# Revit family: Дверь ТДО
name_source: partatom
category: Двери
revit_build: Autodesk Revit 2015 (Build: 20140223_1515(x64)
units: mm (PartAtom-declared; Revit-internal decimal feet)

## types (1)
- Дверь ТДО
    ADSK_URL страницы изделия = http://profholod.ru
    ADSK_Завод-изготовитель = ООО ПрофХолод
    ADSK_Обозначение = ООО ПрофХолод
    ADSK_Открывание = Пр
    URL = http://profholod.ru
    h_porog = 0 мм
    hn_polotno = 8 мм
    Аналитическая конструкция = <Нет>
    Внутренняя сторона = AISI 430-0,5
    Высота = 2200 мм
    Высота в свету = 2168 мм
    Высота порога = 0 мм
    Высота проема до монтажа = 2200 мм
    Высота ручки = 900 мм
    Группа модели = ТДО
    Замыкание стены = По основе
    Изготовитель = ООО ПрофХолод
    Изогнутый отбойник левый = Нет
    Изогнутый отбойник правый = Нет
    Иллюминатор стекло = Пластмасса, прозрачная
    Кирпич = ККС : КРК - к крипичной стене
    Коробка и наличники = RAL9003
    Металл = ККС : МК - к металлоконструкции
    Наружная сторона = RAL9003
    Описание = Двери технологические (ТДО)
    Петли левые = Нет
    Петли правые = Да
    Порог 40 = П : Порог 40
    Порог 40мм = Нет
    Порог 60 = П : Порог 60
    Порог 60мм = Нет
    Резиновые изделия = Резина
    Сендвич = ККС : СП - к сэндвич-панели
    Температурный режим = C
    Тип отбойника = Нет
    Тип порога = П : Без порога
    Толщина полотна = 40 мм
    Функция = Внутренние слои
    Фурнитура = <По категории>
    Ширина = 800 мм
    Ширина в свету = 736 мм
    Ширина проема до монтажа = 800 мм

## geometry (parser evidence)
native form markers: Sweep x4
no freeform markers — native parametric forms only
